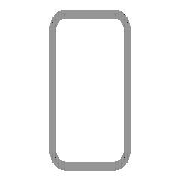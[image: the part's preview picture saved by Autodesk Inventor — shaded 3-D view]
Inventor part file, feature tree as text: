
AUTODESK INVENTOR PART (.ipt)
format: ipt  version: 2025.1 (Build 291241020, 241B)  size: 142,848 bytes
history: native  units: mm (DEFAULTED — no unit token found)
features: other x4, sketch x1, plane x1
ambient origin geometry x8: Origin, YZ Plane, XZ Plane, XY Plane, X Axis, Y Axis, Z Axis, Center Point
bodies: Solid1 (feature_tree), Body (feature_tree)
feature tree (6):
  parser-record x1  (decoder bookkeeping rows leaked as tree rows — omitted from the tree; the rows remain in map.json)
  other  "Driven Length"
  other  "Start Plane"
  other  "End Plane"
  sketch  "Sketch3"  dims[d3=720.0mm d4=0.0mm d7=6.0mm d9=40.0mm d11=60.0mm d12=3.0mm d13=40.0mm d14=760.0mm d15=20.0mm d16=30.0mm d17=90.0deg d18=720.0mm]
  plane  "Work Plane3"
